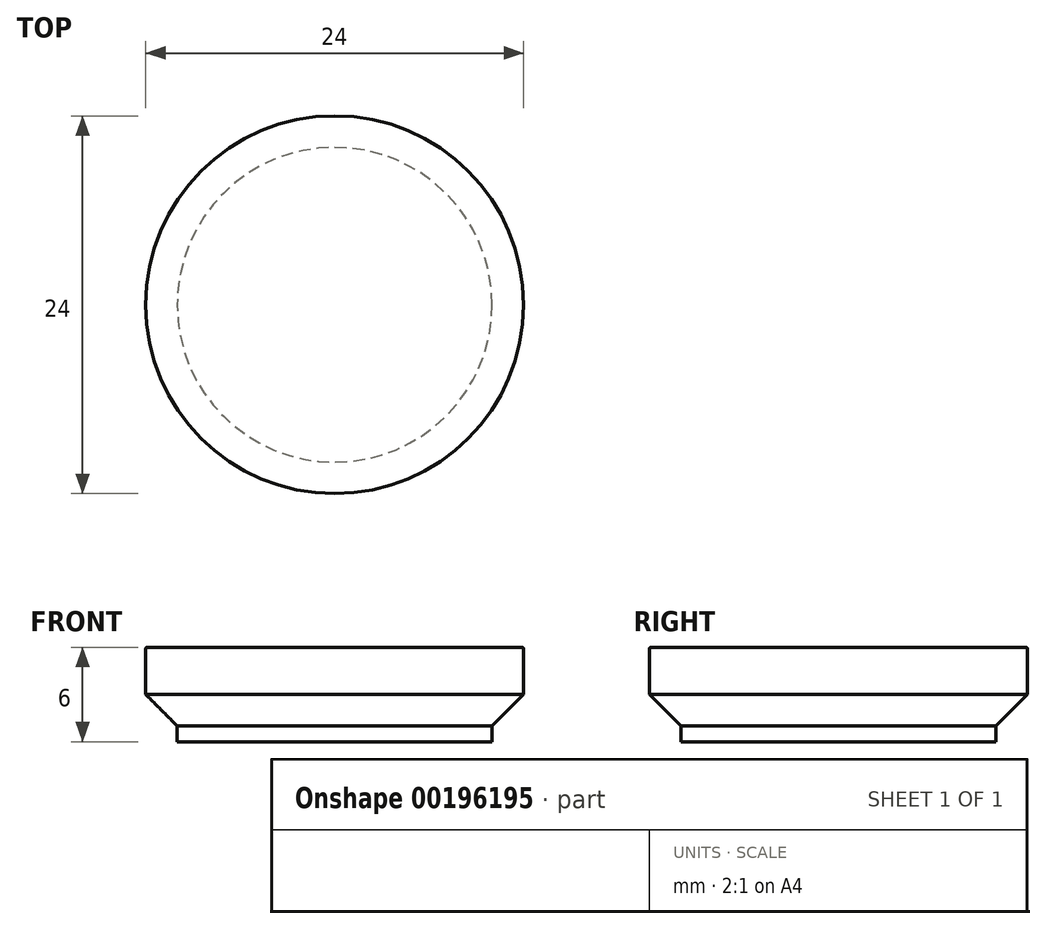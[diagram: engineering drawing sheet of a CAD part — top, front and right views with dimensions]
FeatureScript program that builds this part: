
annotation { "Feature Type Name" : "Feature", "Feature Type Description" : "" }
export const myFeature = defineFeature(function(context is Context, id is Id, definition is map)
    precondition{}
    {
        {
            var Q0;
            Q0=qCreatedBy(makeId("Front.planeOp"),FACE);
            var sketch = newSketch(context, id + "F0", { "sketchPlane" : qUnion([Q0])});
            skLineSegment(sketch, "E0", {"start": v(-8.1, -8.18) * mm, "end": v(-8.1, 8.48) * mm, "construction": true});
            skLineSegment(sketch, "E1", {"start": v(-12, -3) * mm, "end": v(-10, -5) * mm});
            skLineSegment(sketch, "E2", {"start": v(-12, -3) * mm, "end": v(-12, 0) * mm});
            skLineSegment(sketch, "E3", {"start": v(-10, -5) * mm, "end": v(0, -5) * mm, "construction": true});
            skLineSegment(sketch, "E4", {"start": v(-12, 0) * mm, "end": v(0, 0) * mm});
            skLineSegment(sketch, "E5", {"start": v(-10, -5) * mm, "end": v(-10, -6) * mm});
            skLineSegment(sketch, "E6", {"start": v(-10, -6) * mm, "end": v(0, -6) * mm});
            skLineSegment(sketch, "E7", {"start": v(0, -6) * mm, "end": v(0, 0) * mm});
            skSolve(sketch);
        }
        {
            var Q0;
            Q0=makeQuery(id+"F0.imprint","IMPRINT",FACE,{"disambiguationData":[TD([[makeQuery(id+"F0.imprint","IMPRINT",EDGE,{"derivedFrom":sQuery(id+"F0.wireOp",EDGE,"E1")}),1.0]])]});
            var Q1;
            Q1=sQuery(id+"F0.wireOp",EDGE,"E7");
            revolve(context, id + "F1", {"entities" : qUnion([Q0]), "axis" : qUnion([Q1]), "revolveType" : RevolveType.FULL});
        }
        {
            var Q0;
            Q0=makeQuery(id+"F1.opRevolve","SWEPT_EDGE",EDGE,{"disambiguationData":[OSD([sQuery(id+"F0.wireOp",EDGE,"E2"),sQuery(id+"F0.wireOp",EDGE,"E4")])]});
            fillet(context, id + "F2", {"entities" : qUnion([Q0]), "radius" : 0.1 * mm, "tangentPropagation" : true, "allowEdgeOverflow" : false});
        }
    });
